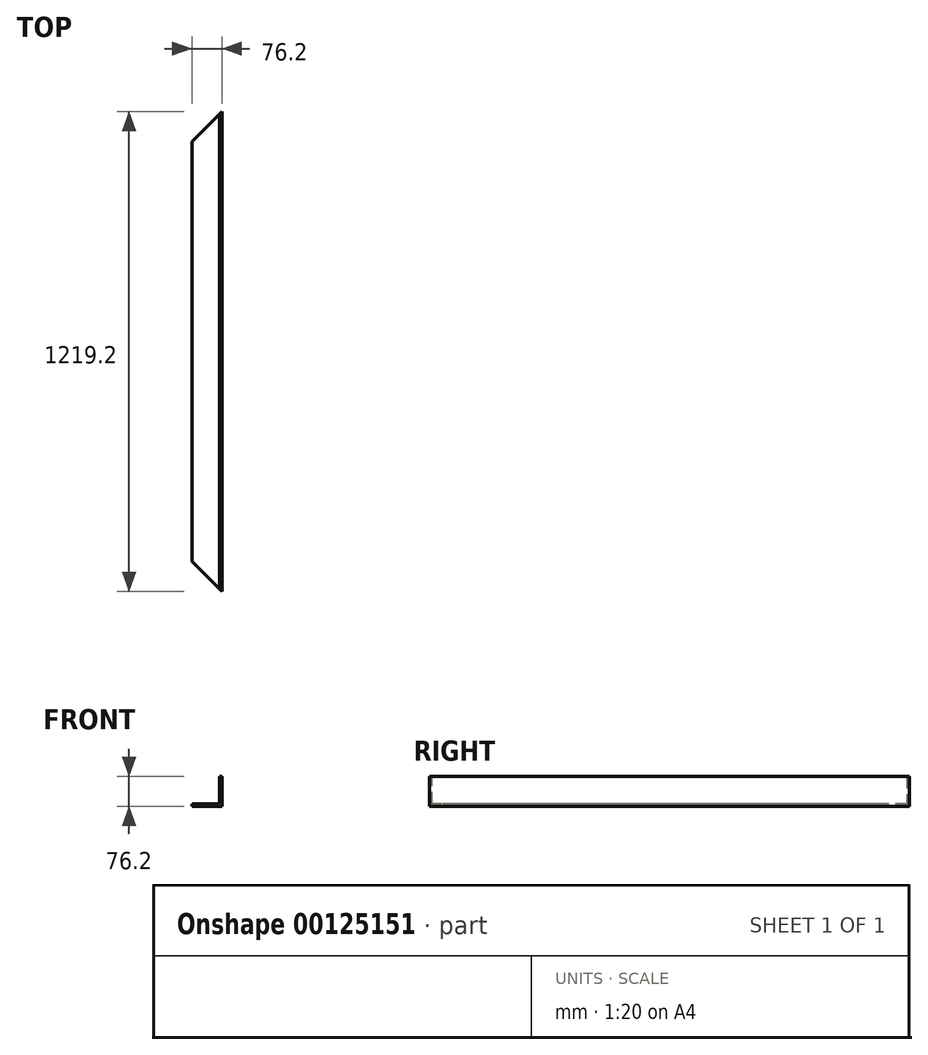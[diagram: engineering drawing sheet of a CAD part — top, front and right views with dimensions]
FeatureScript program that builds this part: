
annotation { "Feature Type Name" : "Feature", "Feature Type Description" : "" }
export const myFeature = defineFeature(function(context is Context, id is Id, definition is map)
    precondition{}
    {
        {
            var Q0;
            Q0=qCreatedBy(makeId("Front.planeOp"),FACE);
            var sketch = newSketch(context, id + "F0", { "sketchPlane" : qUnion([Q0])});
            skLineSegment(sketch, "E0", {"start": v(0, 76.2) * mm, "end": v(0, 0) * mm});
            skLineSegment(sketch, "E1", {"start": v(0, 0) * mm, "end": v(-76.2, 0) * mm});
            skLineSegment(sketch, "E2.0", {"start": v(-6.35, 6.35) * mm, "end": v(-76.2, 6.35) * mm});
            skLineSegment(sketch, "E2.1", {"start": v(-6.35, 76.2) * mm, "end": v(-6.35, 6.35) * mm});
            skLineSegment(sketch, "E3", {"start": v(-76.2, 6.35) * mm, "end": v(-76.2, 0) * mm});
            skLineSegment(sketch, "E4", {"start": v(-6.35, 76.2) * mm, "end": v(0, 76.2) * mm});
            skSolve(sketch);
        }
        {
            var Q0;
            Q0=qSketchRegion(id+"F0",true);
            extrude(context, id + "F1", {"entities" : qUnion([Q0]), "oppositeDirection" : true, "depth" : 1219.2 * mm});
        }
        {
            var Q0;
            Q0=makeQuery(id+"F1.opExtrude","SWEPT_FACE",FACE,{"disambiguationData":[OSD([sQuery(id+"F0.wireOp",EDGE,"E4")])]});
            var sketch = newSketch(context, id + "F2", { "sketchPlane" : qUnion([Q0])});
            skLineSegment(sketch, "E5.0", {"start": v(-76.2, 1219.2) * mm, "end": v(-76.2, 1143) * mm});
            skLineSegment(sketch, "E6", {"start": v(0, 1219.2) * mm, "end": v(-76.2, 1219.2) * mm});
            skLineSegment(sketch, "E7", {"start": v(0, 0) * mm, "end": v(-76.2, 0) * mm});
            skLineSegment(sketch, "E8", {"start": v(0, 1219.2) * mm, "end": v(-76.2, 1143) * mm});
            skLineSegment(sketch, "E9", {"start": v(-76.2, 76.2) * mm, "end": v(0, 0) * mm});
            skLineSegment(sketch, "E10.trimOffspring", {"start": v(-76.2, 76.2) * mm, "end": v(-76.2, 0) * mm});
            skSolve(sketch);
        }
        {
            var Q0;
            Q0=qSketchRegion(id+"F2",true);
            extrude(context, id + "F3", {"entities" : qUnion([Q0]), "operationType" : NewBodyOperationType.REMOVE, "oppositeDirection" : true, "depth" : 76.2 * mm});
        }
    });
